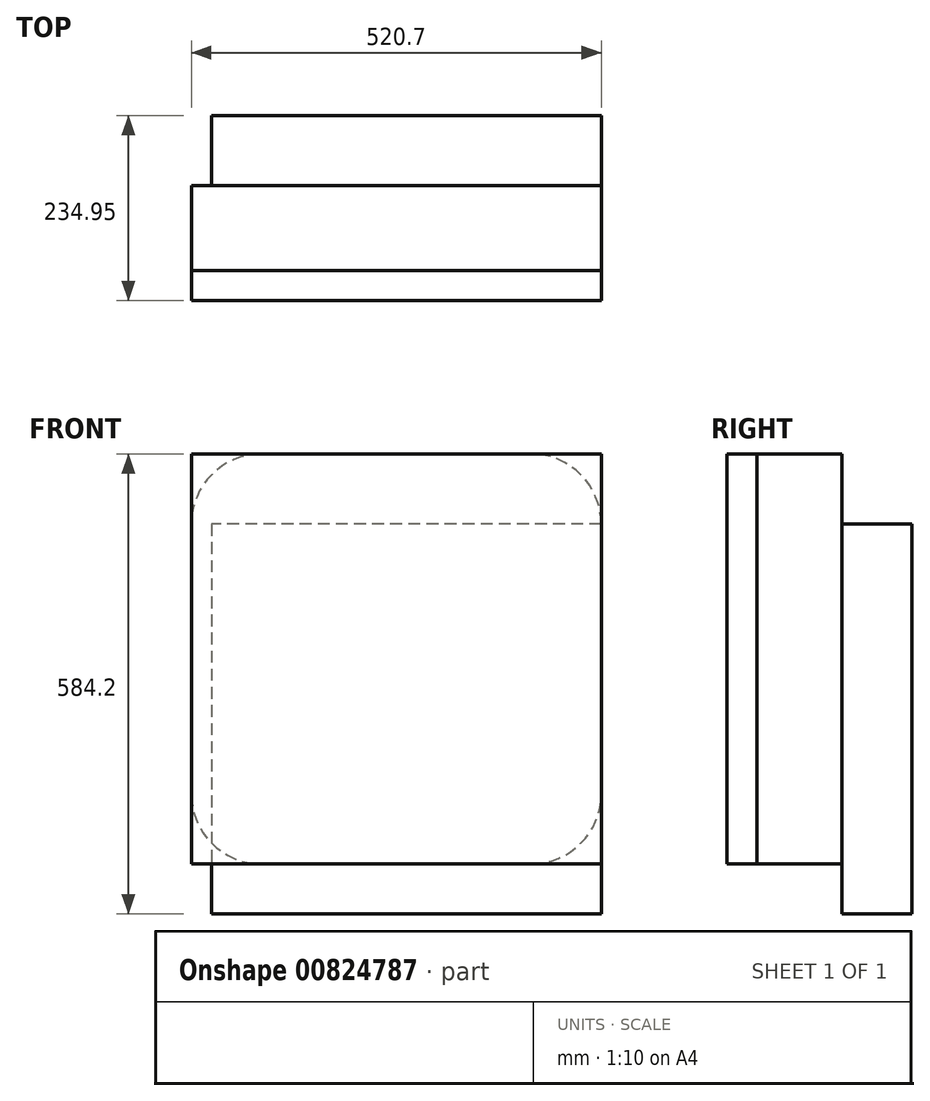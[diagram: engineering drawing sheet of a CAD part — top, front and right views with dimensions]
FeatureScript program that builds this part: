
annotation { "Feature Type Name" : "Feature", "Feature Type Description" : "" }
export const myFeature = defineFeature(function(context is Context, id is Id, definition is map)
    precondition{}
    {
        {
            var Q0;
            Q0=qCreatedBy(makeId("Front.planeOp"),FACE);
            var sketch = newSketch(context, id + "F0", { "sketchPlane" : qUnion([Q0])});
            skLineSegment(sketch, "E0", {"start": v(-333.74, -255.36) * mm, "end": v(-333.74, 265.34) * mm});
            skLineSegment(sketch, "E1", {"start": v(-333.74, 265.34) * mm, "end": v(186.96, 265.34) * mm});
            skLineSegment(sketch, "E2", {"start": v(186.96, 265.34) * mm, "end": v(186.96, -255.36) * mm});
            skLineSegment(sketch, "E3", {"start": v(186.96, -255.36) * mm, "end": v(-333.74, -255.36) * mm});
            skSolve(sketch);
        }
        {
            var Q0;
            Q0 = qSketchRegion(id + "F0", true);
            extrude(context, id + "F1", {"entities" : qUnion([Q0]), "oppositeDirection" : true, "depth" : 107.95 * mm, "offsetDistance" : 25.4 * mm});
        }
        {
            var Q0;
            Q0=makeQuery(id+"F1.opExtrude","SWEPT_EDGE",EDGE,{"disambiguationData":[OSD([sQuery(id+"F0.wireOp",EDGE,"E1"),sQuery(id+"F0.wireOp",EDGE,"E2")])]});
            var Q1;
            Q1=makeQuery(id+"F1.opExtrude","SWEPT_EDGE",EDGE,{"disambiguationData":[OSD([sQuery(id+"F0.wireOp",EDGE,"E2"),sQuery(id+"F0.wireOp",EDGE,"E3")])]});
            var Q2;
            Q2=makeQuery(id+"F1.opExtrude","SWEPT_EDGE",EDGE,{"disambiguationData":[OSD([sQuery(id+"F0.wireOp",EDGE,"E0"),sQuery(id+"F0.wireOp",EDGE,"E3")])]});
            var Q3;
            Q3=makeQuery(id+"F1.opExtrude","SWEPT_EDGE",EDGE,{"disambiguationData":[OSD([sQuery(id+"F0.wireOp",EDGE,"E0"),sQuery(id+"F0.wireOp",EDGE,"E1")])]});
            fillet(context, id + "F2", {"entities" : qUnion([Q0, Q1, Q2, Q3]), "radius" : 88.9 * mm, "tangentPropagation" : true, "allowEdgeOverflow" : false});
        }
        {
            var Q0;
            Q0=makeQuery(id+"F1.opExtrude","CAP_FACE",FACE,{"disambiguationData":[OSD([sQuery(id+"F0.wireOp",EDGE,"E0"),sQuery(id+"F0.wireOp",EDGE,"E1"),sQuery(id+"F0.wireOp",EDGE,"E2"),sQuery(id+"F0.wireOp",EDGE,"E3")])],"isStart":false});
            var sketch = newSketch(context, id + "F3", { "sketchPlane" : qUnion([Q0])});
            skLineSegment(sketch, "E4", {"start": v(-186.96, 176.44) * mm, "end": v(308.34, 176.44) * mm});
            skLineSegment(sketch, "E5", {"start": v(308.34, 176.44) * mm, "end": v(308.34, -318.86) * mm});
            skLineSegment(sketch, "E6", {"start": v(308.34, -318.86) * mm, "end": v(-186.96, -318.86) * mm});
            skLineSegment(sketch, "E7", {"start": v(-186.96, -318.86) * mm, "end": v(-186.96, 176.44) * mm});
            skSolve(sketch);
        }
        {
            var Q0;
            {var subQ6=sQuery(id+"F3.wireOp",EDGE,"E6");Q0=makeQuery(id+"F3.imprint","IMPRINT",FACE,{"disambiguationData":[TD([[makeQuery(id+"F3.imprint","IMPRINT",EDGE,{"derivedFrom":subQ6}),-1.0]])]});}
            var Q1;
            {var subQ7=sQuery(id+"F3.wireOp",EDGE,"E4");Q1=makeQuery(id+"F3.imprint","IMPRINT",FACE,{"disambiguationData":[TD([[makeQuery(id+"F3.imprint","IMPRINT",EDGE,{"derivedFrom":subQ7}),-1.0]])]});}
            extrude(context, id + "F4", {"entities" : qUnion([Q0, Q1]), "depth" : 88.9 * mm, "offsetDistance" : 25.4 * mm});
        }
        {
            var Q0;
            Q0=makeQuery(id+"F1.opExtrude","CAP_FACE",FACE,{"disambiguationData":[OSD([sQuery(id+"F0.wireOp",EDGE,"E0"),sQuery(id+"F0.wireOp",EDGE,"E1"),sQuery(id+"F0.wireOp",EDGE,"E2"),sQuery(id+"F0.wireOp",EDGE,"E3")])],"isStart":true});
            var sketch = newSketch(context, id + "F5", { "sketchPlane" : qUnion([Q0])});
            skLineSegment(sketch, "E8", {"start": v(-333.74, -255.36) * mm, "end": v(186.96, -255.36) * mm});
            skLineSegment(sketch, "E9", {"start": v(186.96, -255.36) * mm, "end": v(186.96, 265.34) * mm});
            skLineSegment(sketch, "E10", {"start": v(186.96, 265.34) * mm, "end": v(-333.74, 265.34) * mm});
            skLineSegment(sketch, "E11", {"start": v(-333.74, 265.34) * mm, "end": v(-333.74, -255.36) * mm});
            skSolve(sketch);
        }
        {
            var Q0;
            {var subQ9=sQuery(id+"F5.wireOp",EDGE,"E9");Q0=makeQuery(id+"F5.imprint","IMPRINT",FACE,{"disambiguationData":[TD([[makeQuery(id+"F5.imprint","IMPRINT",EDGE,{"derivedFrom":subQ9}),1.0]])]});}
            var Q1;
            {var subQ0=sQuery(id+"F5.wireOp",EDGE,"E11");var subQ1=sQuery(id+"F5.wireOp",EDGE,"E8");var subQ2=makeQuery(id+"F5.imprint","INTERSECT",VERTEX,{"derivedFrom":[subQ1,subQ0]});Q1=makeQuery(id+"F5.imprint","IMPRINT",FACE,{"disambiguationData":[TD([[makeQuery(id+"F5.imprint","IMPRINT",EDGE,{"disambiguationData":[TD([[subQ2,-1.0]])],"derivedFrom":subQ1}),1.0]])]});}
            var Q2;
            {var subQ1=sQuery(id+"F0.wireOp",EDGE,"E1");var subQ2=sQuery(id+"F0.wireOp",EDGE,"E0");var subQ3=makeQuery(id+"F2.opFillet","BLEND_EDGE",EDGE,{"blendedFrom":[makeQuery(id+"F1.opExtrude","SWEPT_EDGE",EDGE,{"disambiguationData":[OSD([subQ2,subQ1])]}),makeQuery(id+"F1.opExtrude","CAP_FACE",FACE,{"disambiguationData":[OSD([subQ2,subQ1,sQuery(id+"F0.wireOp",EDGE,"E2"),sQuery(id+"F0.wireOp",EDGE,"E3")])],"isStart":true})],"blendedInto":[makeQuery(id+"F1.opExtrude","CAP_FACE",FACE,{"disambiguationData":[OSD([subQ2,subQ1,sQuery(id+"F0.wireOp",EDGE,"E2"),sQuery(id+"F0.wireOp",EDGE,"E3")])],"isStart":true})]});Q2=makeQuery(id+"F5.imprint","IMPRINT",FACE,{"disambiguationData":[TD([[makeQuery(id+"F5.imprint","IMPRINT",EDGE,{"derivedFrom":subQ3}),-1.0]])]});}
            var Q3;
            {var subQ1=sQuery(id+"F0.wireOp",EDGE,"E3");var subQ2=sQuery(id+"F0.wireOp",EDGE,"E2");var subQ3=sQuery(id+"F0.wireOp",EDGE,"E1");var subQ4=sQuery(id+"F0.wireOp",EDGE,"E0");var subQ5=makeQuery(id+"F1.opExtrude","CAP_FACE",FACE,{"disambiguationData":[OSD([subQ4,subQ3,subQ2,subQ1])],"isStart":true});var subQ6=makeQuery(id+"F2.opFillet","BLEND_EDGE",EDGE,{"blendedFrom":[makeQuery(id+"F1.opExtrude","SWEPT_EDGE",EDGE,{"disambiguationData":[OSD([subQ4,subQ1])]}),subQ5],"blendedInto":[subQ5]});Q3=makeQuery(id+"F5.imprint","IMPRINT",FACE,{"disambiguationData":[TD([[makeQuery(id+"F5.imprint","IMPRINT",EDGE,{"derivedFrom":subQ6}),1.0]])]});}
            extrude(context, id + "F6", {"entities" : qUnion([Q0, Q1, Q2, Q3]), "depth" : 38.1 * mm, "offsetDistance" : 25.4 * mm});
        }
    });
